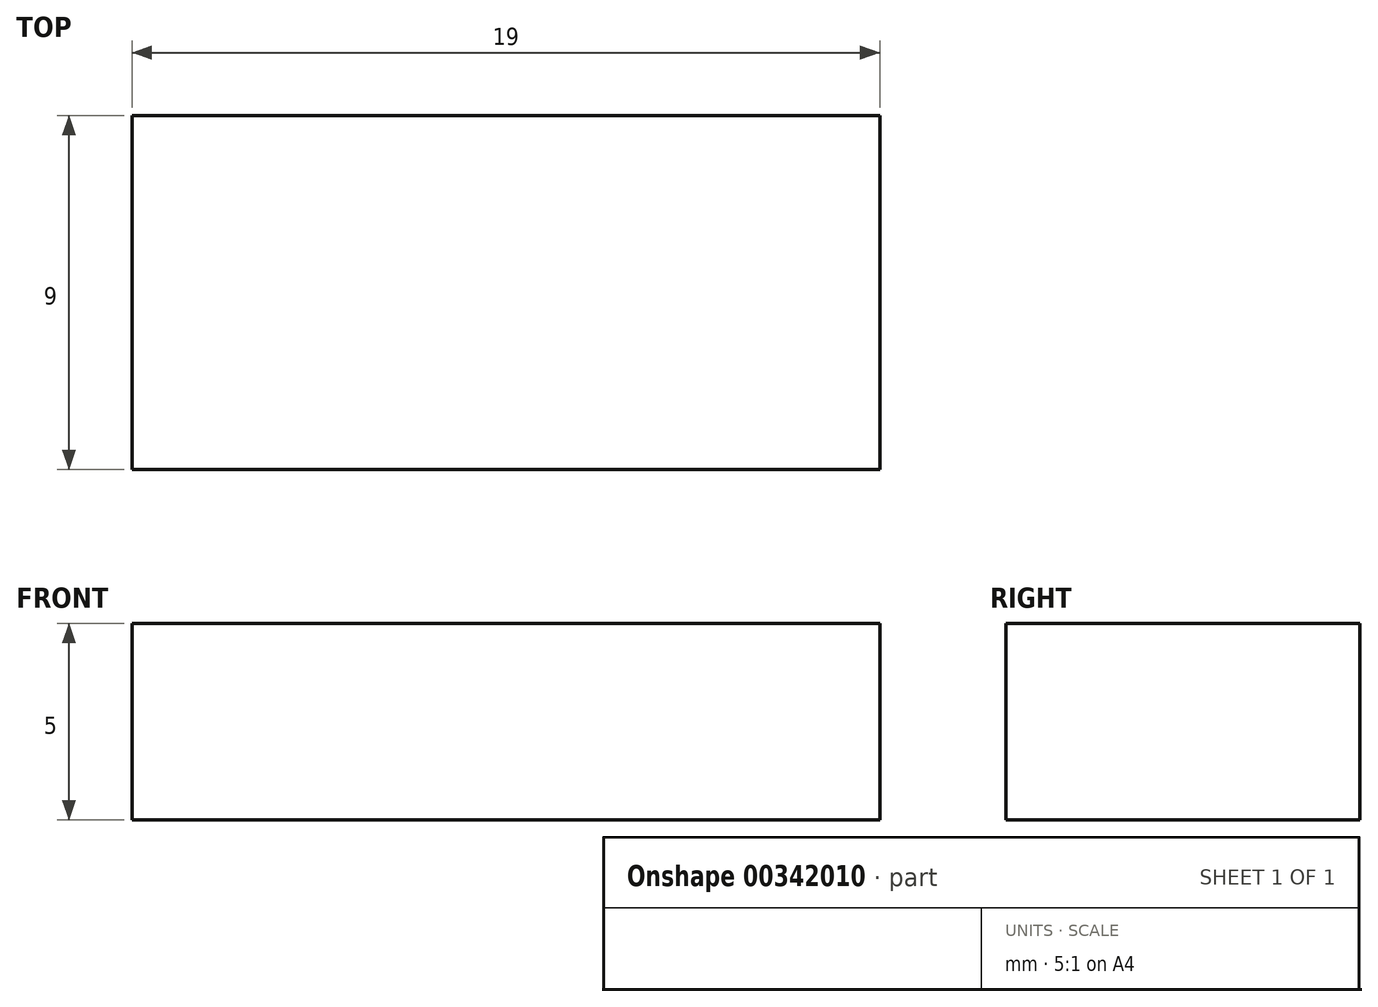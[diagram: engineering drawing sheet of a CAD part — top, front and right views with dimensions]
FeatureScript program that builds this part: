
annotation { "Feature Type Name" : "Feature", "Feature Type Description" : "" }
export const myFeature = defineFeature(function(context is Context, id is Id, definition is map)
    precondition{}
    {
        {
            var Q0;
            Q0=qCreatedBy(makeId("Top.planeOp"),FACE);
            var sketch = newSketch(context, id + "F0", { "sketchPlane" : qUnion([Q0])});
            skLineSegment(sketch, "E0.bottom", {"start": v(0, 0) * mm, "end": v(19, 0) * mm});
            skLineSegment(sketch, "E0.top", {"start": v(0, 9) * mm, "end": v(19, 9) * mm});
            skLineSegment(sketch, "E0.left", {"start": v(0, 0) * mm, "end": v(0, 9) * mm});
            skLineSegment(sketch, "E0.right", {"start": v(19, 0) * mm, "end": v(19, 9) * mm});
            skSolve(sketch);
        }
        {
            var Q0;
            Q0=makeQuery(id+"F0.imprint","IMPRINT",FACE,{"disambiguationData":[TD([[makeQuery(id+"F0.imprint","IMPRINT",EDGE,{"derivedFrom":sQuery(id+"F0.wireOp",EDGE,"E0.bottom")}),1.0]])]});
            extrude(context, id + "F1", {"entities" : qUnion([Q0]), "depth" : 5 * mm});
        }
    });
